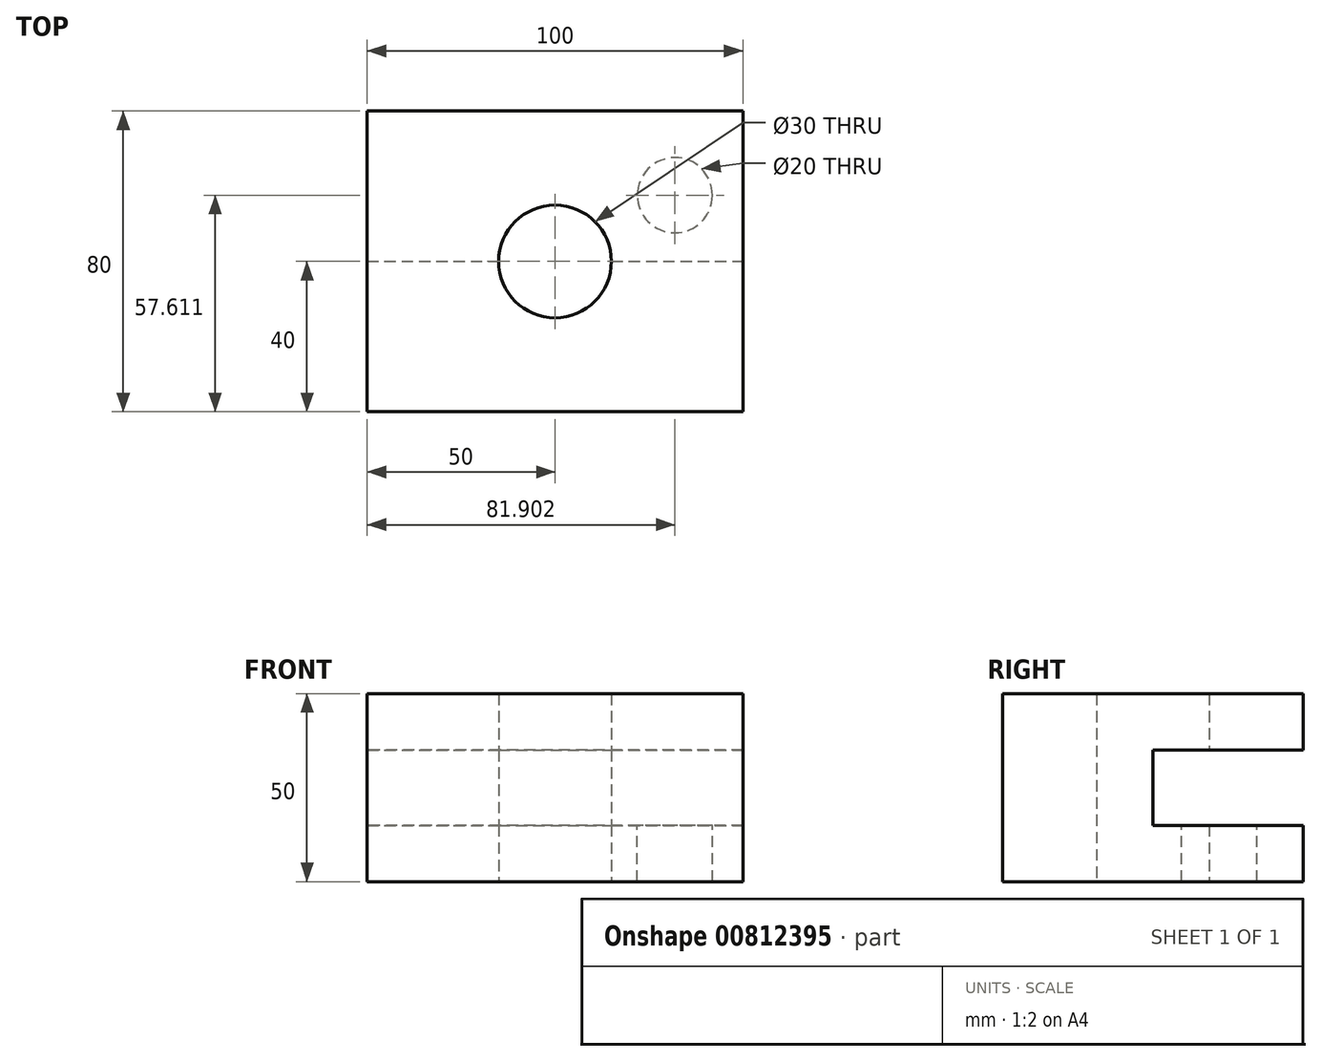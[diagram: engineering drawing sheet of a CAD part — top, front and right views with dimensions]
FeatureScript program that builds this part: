
annotation { "Feature Type Name" : "Feature", "Feature Type Description" : "" }
export const myFeature = defineFeature(function(context is Context, id is Id, definition is map)
    precondition{}
    {
        {
            var Q0;
            Q0=qCreatedBy(makeId("Top.planeOp"),FACE);
            var sketch = newSketch(context, id + "F0", { "sketchPlane" : qUnion([Q0])});
            skLineSegment(sketch, "E0.bottom", {"start": v(-50, 40) * mm, "end": v(50, 40) * mm});
            skLineSegment(sketch, "E0.top", {"start": v(-50, -40) * mm, "end": v(50, -40) * mm});
            skLineSegment(sketch, "E0.left", {"start": v(-50, 40) * mm, "end": v(-50, -40) * mm});
            skLineSegment(sketch, "E0.right", {"start": v(50, 40) * mm, "end": v(50, -40) * mm});
            skCircle(sketch, "E1", {"center": v(0, 0) * mm, "radius": 15 * mm});
            skSolve(sketch);
        }
        {
            var Q0;
            Q0 = qSketchRegion(id + "F0", true);
            extrude(context, id + "F1", {"entities" : qUnion([Q0]), "depth" : 50 * mm, "offsetDistance" : 25.4 * mm});
        }
        {
            var Q0;
            Q0=qCreatedBy(makeId("Front.planeOp"),FACE);
            var sketch = newSketch(context, id + "F2", { "sketchPlane" : qUnion([Q0])});
            skLineSegment(sketch, "E2.bottom", {"start": v(-50, 35) * mm, "end": v(50, 35) * mm});
            skLineSegment(sketch, "E2.top", {"start": v(-50, 15) * mm, "end": v(50, 15) * mm});
            skLineSegment(sketch, "E2.left", {"start": v(-50, 35) * mm, "end": v(-50, 15) * mm});
            skLineSegment(sketch, "E2.right", {"start": v(50, 35) * mm, "end": v(50, 15) * mm});
            skLineSegment(sketch, "E3", {"start": v(-58.32, 0) * mm, "end": v(10.54, 0) * mm});
            skSolve(sketch);
        }
        {
            var Q0;
            Q0 = qSketchRegion(id + "F2", true);
            extrude(context, id + "F3", {"entities" : qUnion([Q0]), "operationType" : NewBodyOperationType.REMOVE, "oppositeDirection" : true, "depth" : 50 * mm, "offsetDistance" : 25 * mm});
        }
        {
            var Q0;
            Q0=makeQuery(id+"F3.boolean.opBoolean","COPY",FACE,{"derivedFrom":makeQuery(id+"F3.opExtrude","SWEPT_FACE",FACE,{"disambiguationData":[OSD([sQuery(id+"F2.wireOp",EDGE,"E2.top")])]})});
            var sketch = newSketch(context, id + "F4", { "sketchPlane" : qUnion([Q0])});
            skCircle(sketch, "E4", {"center": v(31.9, 17.61) * mm, "radius": 10 * mm});
            skSolve(sketch);
        }
        {
            var Q0;
            Q0 = qSketchRegion(id + "F4", true);
            extrude(context, id + "F5", {"entities" : qUnion([Q0]), "operationType" : NewBodyOperationType.REMOVE, "endBound" : BoundingType.UP_TO_NEXT, "oppositeDirection" : true, "depth" : 25 * mm, "offsetDistance" : 25 * mm});
        }
    });
